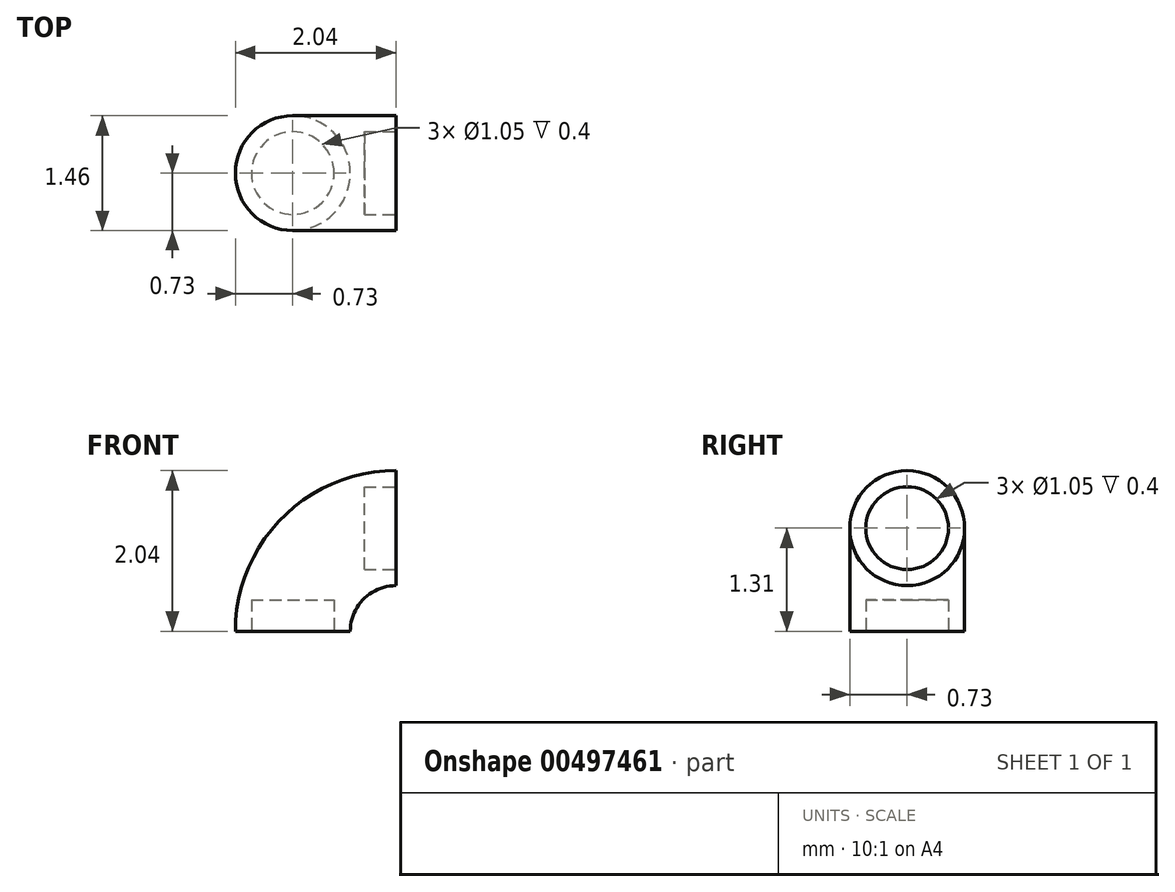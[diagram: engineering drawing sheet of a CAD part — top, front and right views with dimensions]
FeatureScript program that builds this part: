
annotation { "Feature Type Name" : "Feature", "Feature Type Description" : "" }
export const myFeature = defineFeature(function(context is Context, id is Id, definition is map)
    precondition{}
    {
        {
            var Q0;
            Q0=qCreatedBy(makeId("Top.planeOp"),FACE);
            var sketch = newSketch(context, id + "F0", { "sketchPlane" : qUnion([Q0])});
            skCircle(sketch, "E0", {"center": v(0, 0) * mm, "radius": 0.73 * mm});
            skLineSegment(sketch, "E1", {"start": v(0, 0) * mm, "end": v(1.31, 0) * mm});
            skLineSegment(sketch, "E2", {"start": v(1.31, 0) * mm, "end": v(1.31, 0.62) * mm});
            skSolve(sketch);
        }
        {
            var Q0;
            Q0=makeQuery(id+"F0.imprint","IMPRINT",FACE,{"disambiguationData":[TD([[makeQuery(id+"F0.imprint","IMPRINT",EDGE,{"derivedFrom":sQuery(id+"F0.wireOp",EDGE,"E0")}),1.0]])]});
            var Q1;
            Q1=sQuery(id+"F0.wireOp",EDGE,"E2");
            revolve(context, id + "F1", {"entities" : qUnion([Q0]), "axis" : qUnion([Q1]), "revolveType" : RevolveType.ONE_DIRECTION, "angle" : 90 * degree});
        }
        {
            var Q0;
            Q0=makeQuery(id+"F1.opRevolve","CAP_FACE",FACE,{"disambiguationData":[OSD([sQuery(id+"F0.wireOp",EDGE,"E0")])],"isStart":false});
            var sketch = newSketch(context, id + "F2", { "sketchPlane" : qUnion([Q0])});
            skCircle(sketch, "E3", {"center": v(0, 1.31) * mm, "radius": 0.53 * mm});
            skSolve(sketch);
        }
        {
            var Q0;
            Q0=makeQuery(id+"F2.imprint","IMPRINT",FACE,{"disambiguationData":[TD([[makeQuery(id+"F2.imprint","IMPRINT",EDGE,{"derivedFrom":sQuery(id+"F2.wireOp",EDGE,"E3")}),1.0]])]});
            extrude(context, id + "F3", {"entities" : qUnion([Q0]), "operationType" : NewBodyOperationType.REMOVE, "oppositeDirection" : true, "depth" : .4 * mm});
        }
        {
            var Q0;
            Q0=makeQuery(id+"F1.opRevolve","CAP_FACE",FACE,{"disambiguationData":[OSD([sQuery(id+"F0.wireOp",EDGE,"E0")])],"isStart":true});
            var sketch = newSketch(context, id + "F4", { "sketchPlane" : qUnion([Q0])});
            skCircle(sketch, "E4", {"center": v(0, 0) * mm, "radius": 0.53 * mm});
            skSolve(sketch);
        }
        {
            var Q0;
            Q0 = qSketchRegion(id + "F4", true);
            extrude(context, id + "F5", {"entities" : qUnion([Q0]), "operationType" : NewBodyOperationType.REMOVE, "oppositeDirection" : true, "depth" : .4 * mm});
        }
    });
